# Revit family: Window_Fixed_Flush_Ready-Access_603-WalkUp
name_source: partatom
category: Windows
units: mm (PartAtom-declared; Revit-internal decimal feet)

## family parameters
Always vertical = Yes
Classification Number = 23.30.20.24.21
Cut with Voids When Loaded = No
Host = Wall
Room Calculation Point = No
Shared = No

## types (9) — shared parameters
Air Infiltration = as Specified
Assembly Code = B2020100
Construction Details = http://www.arcat.com
Description = Ready Access Fixed Secure Transaction Window - 603 Walk Up as Specified
Forced Entry Rating = as Specified
Frame Thickness = 0' - 4 1/2"
Keynote = 08582
Manufacturer = Ready Access
Manufacturer Fax = 630-876-7767
Manufacturer Website = http://www.ready-access.com
Meets Egress = as Specified
Miami Dade Conformance = as Specified
Product Data = http://www.arcat.com
Sales Information = http://www.ready-access.com
Send Message = http://www.arcat.com
Service Opening Height = 0' - 0"
Service Opening Width = 0' - 0"
Specification = http://www.arcat.com
Standards Conformance = as Specified
Structural Test Pressure = as Specified
URL = http://www.ready-access.com
Wall Closure = By host
Water Penetration = as Specified
zero-valued in all types: Expected Lifespan (Years), Maintenance Schedule (Months), Sound Transmission Class (STC), Warranty Duration (Years)

## per-type parameters (varying)
| type | Height | Model | Shelf Width | Width |
| 48x48 Level 3 Bullet | 4' - 0" | 603 WALK UP 48 | 4' - 0" | 4' - 0" |
| 36x36 Level 3 Bullet | 3' - 0" | 603 WALK UP 36 | 3' - 0" | 3' - 0" |
| 25.75x42 Level 3 Bullet | 3' - 6" | 603 WALK UP 42 | 2' - 1 3/4" | 2' - 1 3/4" |
| 48x48 Level 1 Bullet | 4' - 0" | 603 WALK UP 48 | 4' - 0" | 4' - 0" |
| 36x36 Level 1 Bullet | 3' - 0" | 603 WALK UP 36 | 3' - 0" | 3' - 0" |
| 25.75x42 Level 1 Bullet | 3' - 6" | 603 WALK UP 42 | 2' - 1 3/4" | 2' - 1 3/4" |
| 48x48 Impact Resistant | 4' - 0" | 603 WALK UP 48 | 4' - 0" | 4' - 0" |
| 36x36 Impact Resistant | 3' - 0" | 603 WALK UP 36 | 3' - 0" | 3' - 0" |
| 25.75x42 Impact Resistant | 3' - 6" | 603 WALK UP 42 | 2' - 1 3/4" | 2' - 1 3/4" |

## geometry (parser evidence)
native form markers: Sweep x3
no freeform markers — native parametric forms only
